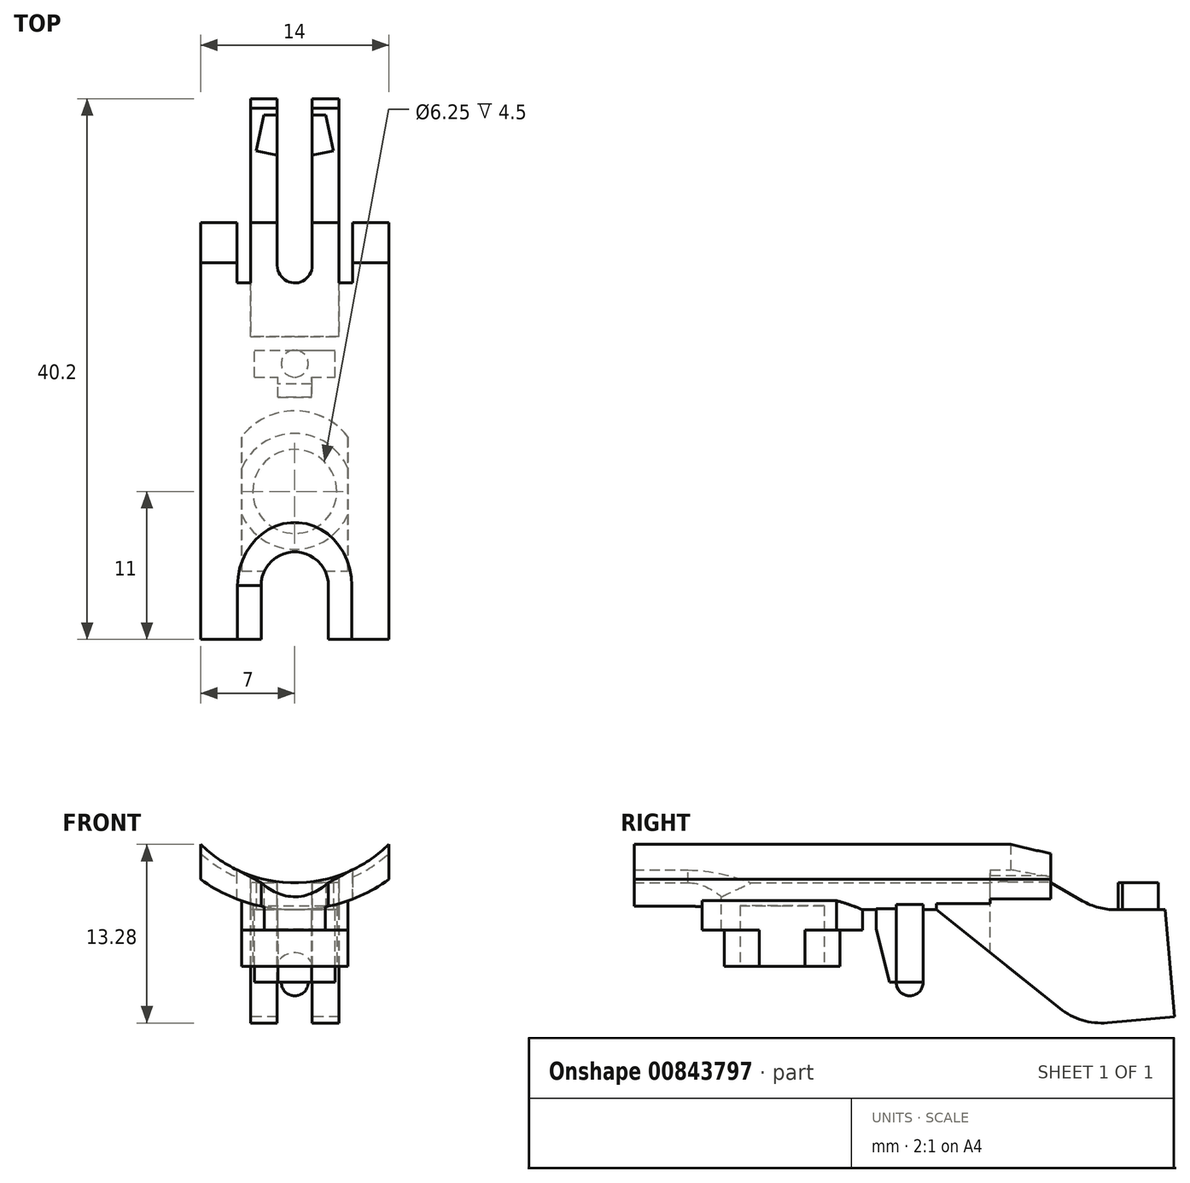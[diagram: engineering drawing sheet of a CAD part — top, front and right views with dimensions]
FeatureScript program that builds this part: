
annotation { "Feature Type Name" : "Feature", "Feature Type Description" : "" }
export const myFeature = defineFeature(function(context is Context, id is Id, definition is map)
    precondition{}
    {
        {
            var Q0;
            Q0=qCreatedBy(makeId("Front.planeOp"),FACE);
            var sketch = newSketch(context, id + "F0", { "sketchPlane" : qUnion([Q0])});
            skArc(sketch, "E0", {"start": v(-7, -7.14) * mm, "mid": v(0, -10) * mm, "end": v(7, -7.14) * mm});
            skLineSegment(sketch, "E1", {"start": v(-7, -11.98) * mm, "end": v(-7, 0) * mm, "construction": true});
            skLineSegment(sketch, "E2", {"start": v(-7, 0) * mm, "end": v(7, 0) * mm, "construction": true});
            skLineSegment(sketch, "E3", {"start": v(7, 0) * mm, "end": v(7, -11.98) * mm, "construction": true});
            skArc(sketch, "E4.0", {"start": v(-7, -9.75) * mm, "mid": v(0, -12) * mm, "end": v(7, -9.75) * mm});
            skLineSegment(sketch, "E5", {"start": v(-7, -9.75) * mm, "end": v(-7, -7.14) * mm});
            skLineSegment(sketch, "E6", {"start": v(7, -7.14) * mm, "end": v(7, -9.75) * mm});
            skSolve(sketch);
        }
        {
            var Q0;
            Q0=makeQuery(id+"F0.imprint","IMPRINT",FACE,{"disambiguationData":[TD([[makeQuery(id+"F0.imprint","IMPRINT",EDGE,{"derivedFrom":sQuery(id+"F0.wireOp",EDGE,"E0")}),-1.0]])]});
            extrude(context, id + "F1", {"entities" : qUnion([Q0]), "endBound" : BoundingType.SYMMETRIC, "depth" : 31 * mm, "offsetDistance" : 25 * mm});
        }
        {
            var Q0;
            Q0=qCreatedBy(makeId("Top.planeOp"),FACE);
            var sketch = newSketch(context, id + "F2", { "sketchPlane" : qUnion([Q0])});
            skArc(sketch, "E7", {"start": v(2.5, -11.5) * mm, "mid": v(0, -9) * mm, "end": v(-2.5, -11.5) * mm});
            skLineSegment(sketch, "E8", {"start": v(-2.5, -11.5) * mm, "end": v(-2.5, -15.5) * mm});
            skLineSegment(sketch, "E9", {"start": v(-2.5, -15.5) * mm, "end": v(2.5, -15.5) * mm});
            skLineSegment(sketch, "E10", {"start": v(2.5, -15.5) * mm, "end": v(2.5, -11.5) * mm});
            skSolve(sketch);
        }
        {
            var Q0;
            Q0=qCreatedBy(makeId("Top.planeOp"),FACE);
            cPlane(context, id + "F3", {"entities" : qUnion([Q0]), "cplaneType" : CPlaneType.OFFSET, "offset" : 10 * mm, "oppositeDirection" : true, "width" : 150 * mm, "height" : 150 * mm});
        }
        {
            var Q0;
            Q0=qCreatedBy(id+"F3.planeOp",FACE);
            var sketch = newSketch(context, id + "F4", { "sketchPlane" : qUnion([Q0])});
            skLineSegment(sketch, "E11", {"start": v(-3.95, -0.43) * mm, "end": v(-3.95, -10.43) * mm});
            skLineSegment(sketch, "E12", {"start": v(-3.95, -10.43) * mm, "end": v(3.95, -10.43) * mm});
            skArc(sketch, "E13", {"start": v(3.95, -0.43) * mm, "mid": v(0, 1.5) * mm, "end": v(-3.95, -0.43) * mm});
            skLineSegment(sketch, "E14", {"start": v(3.95, -0.43) * mm, "end": v(3.95, -10.43) * mm});
            skSolve(sketch);
        }
        {
            var Q0;
            Q0=makeQuery(id+"F4.imprint","IMPRINT",FACE,{"disambiguationData":[TD([[makeQuery(id+"F4.imprint","IMPRINT",EDGE,{"derivedFrom":sQuery(id+"F4.wireOp",EDGE,"E11")}),1.0]])]});
            extrude(context, id + "F5", {"entities" : qUnion([Q0]), "operationType" : NewBodyOperationType.ADD, "oppositeDirection" : true, "depth" : 3.5 * mm, "offsetDistance" : 25 * mm});
        }
        {
            var Q0;
            Q0=makeQuery(id+"F2.imprint","IMPRINT",FACE,{"disambiguationData":[TD([[makeQuery(id+"F2.imprint","IMPRINT",EDGE,{"derivedFrom":sQuery(id+"F2.wireOp",EDGE,"E7")}),1.0]])]});
            extrude(context, id + "F6", {"entities" : qUnion([Q0]), "operationType" : NewBodyOperationType.REMOVE, "endBound" : BoundingType.THROUGH_ALL, "oppositeDirection" : true, "depth" : 25 * mm, "offsetDistance" : 25 * mm});
        }
        {
            var Q0;
            Q0=makeQuery(id+"F6.boolean.opBoolean","INTERSECT",EDGE,{"derivedFrom":[makeQuery(id+"F1.opExtrude","SWEPT_FACE",FACE,{"disambiguationData":[OSD([sQuery(id+"F0.wireOp",EDGE,"E0")])]}),makeQuery(id+"F6.opExtrude","SWEPT_FACE",FACE,{"disambiguationData":[OSD([sQuery(id+"F2.wireOp",EDGE,"E8")])]})]});
            var Q1;
            Q1=makeQuery(id+"F6.boolean.opBoolean","INTERSECT",EDGE,{"derivedFrom":[makeQuery(id+"F1.opExtrude","SWEPT_FACE",FACE,{"disambiguationData":[OSD([sQuery(id+"F0.wireOp",EDGE,"E0")])]}),makeQuery(id+"F6.opExtrude","SWEPT_FACE",FACE,{"disambiguationData":[OSD([sQuery(id+"F2.wireOp",EDGE,"E7")])]})]});
            var Q2;
            Q2=makeQuery(id+"F6.boolean.opBoolean","INTERSECT",EDGE,{"derivedFrom":[makeQuery(id+"F1.opExtrude","SWEPT_FACE",FACE,{"disambiguationData":[OSD([sQuery(id+"F0.wireOp",EDGE,"E0")])]}),makeQuery(id+"F6.opExtrude","SWEPT_FACE",FACE,{"disambiguationData":[OSD([sQuery(id+"F2.wireOp",EDGE,"E10")])]})]});
            chamfer(context, id + "F7", {"entities" : qUnion([Q0, Q1, Q2]), "chamferType" : ChamferType.TWO_OFFSETS, "width1" : .5 * mm, "oppositeDirection" : false, "width2" : 2 * mm, "tangentPropagation" : true});
        }
        {
            var Q0;
            Q0=qCreatedBy(id+"F3.planeOp",FACE);
            var sketch = newSketch(context, id + "F8", { "sketchPlane" : qUnion([Q0])});
            skLineSegment(sketch, "E15.bottom", {"start": v(-3, 6) * mm, "end": v(3, 6) * mm});
            skLineSegment(sketch, "E15.top", {"start": v(-3, 4) * mm, "end": v(-1.25, 4) * mm});
            skLineSegment(sketch, "E15.left", {"start": v(-3, 6) * mm, "end": v(-3, 4) * mm});
            skLineSegment(sketch, "E15.right", {"start": v(3, 6) * mm, "end": v(3, 4) * mm});
            skLineSegment(sketch, "E16", {"start": v(1.25, 4) * mm, "end": v(1.25, 2.5) * mm});
            skLineSegment(sketch, "E17", {"start": v(1.25, 2.5) * mm, "end": v(-1.25, 2.5) * mm});
            skLineSegment(sketch, "E18", {"start": v(-1.25, 2.5) * mm, "end": v(-1.25, 4) * mm});
            skLineSegment(sketch, "E19.trimOffspring", {"start": v(1.25, 4) * mm, "end": v(3, 4) * mm});
            skSolve(sketch);
        }
        {
            var Q0;
            Q0 = qSketchRegion(id + "F8", true);
            extrude(context, id + "F9", {"entities" : qUnion([Q0]), "operationType" : NewBodyOperationType.ADD, "oppositeDirection" : true, "depth" : 7.4 * mm, "offsetDistance" : 25 * mm});
        }
        {
            var Q0;
            Q0=qCreatedBy(makeId("Right.planeOp"),FACE);
            var sketch = newSketch(context, id + "F10", { "sketchPlane" : qUnion([Q0])});
            skLineSegment(sketch, "E20", {"start": v(15.5, -10) * mm, "end": v(19, -12) * mm});
            skLineSegment(sketch, "E21", {"start": v(19, -12) * mm, "end": v(24, -12) * mm});
            skLineSegment(sketch, "E22", {"start": v(24, -12) * mm, "end": v(24.7, -19.97) * mm});
            skLineSegment(sketch, "E23", {"start": v(24.7, -19.97) * mm, "end": v(17.72, -20.58) * mm});
            skLineSegment(sketch, "E24", {"start": v(17.72, -20.58) * mm, "end": v(7, -12) * mm});
            skLineSegment(sketch, "E25", {"start": v(7, -12) * mm, "end": v(7, -10) * mm});
            skLineSegment(sketch, "E26", {"start": v(7, -10) * mm, "end": v(15.5, -10) * mm});
            skSolve(sketch);
        }
        {
            var Q0;
            Q0=makeQuery(id+"F10.imprint","IMPRINT",FACE,{"disambiguationData":[TD([[makeQuery(id+"F10.imprint","IMPRINT",EDGE,{"derivedFrom":sQuery(id+"F10.wireOp",EDGE,"E20")}),-1.0]])]});
            extrude(context, id + "F11", {"entities" : qUnion([Q0]), "operationType" : NewBodyOperationType.ADD, "endBound" : BoundingType.SYMMETRIC, "depth" : 6.6 * mm, "offsetDistance" : 25 * mm});
        }
        {
            var Q0;
            Q0=qCreatedBy(makeId("Top.planeOp"),FACE);
            var sketch = newSketch(context, id + "F12", { "sketchPlane" : qUnion([Q0])});
            skLineSegment(sketch, "E27.bottom", {"start": v(-4.3, 11) * mm, "end": v(-3.3, 11) * mm});
            skLineSegment(sketch, "E27.top", {"start": v(-4.3, 20.5) * mm, "end": v(-3.3, 20.5) * mm});
            skLineSegment(sketch, "E27.left", {"start": v(-4.3, 11) * mm, "end": v(-4.3, 20.5) * mm});
            skLineSegment(sketch, "E27.right", {"start": v(-3.3, 11) * mm, "end": v(-3.3, 20.5) * mm});
            skLineSegment(sketch, "E28.bottom", {"start": v(4.3, 20.5) * mm, "end": v(3.3, 20.5) * mm});
            skLineSegment(sketch, "E28.top", {"start": v(4.3, 11) * mm, "end": v(3.3, 11) * mm});
            skLineSegment(sketch, "E28.left", {"start": v(4.3, 20.5) * mm, "end": v(4.3, 11) * mm});
            skLineSegment(sketch, "E28.right", {"start": v(3.3, 20.5) * mm, "end": v(3.3, 11) * mm});
            skLineSegment(sketch, "E29", {"start": v(3.3, 11) * mm, "end": v(0, 11) * mm, "construction": true});
            skLineSegment(sketch, "E30", {"start": v(0, 11) * mm, "end": v(-3.3, 11) * mm, "construction": true});
            skArc(sketch, "E31", {"start": v(-1.3, 12.3) * mm, "mid": v(0, 11) * mm, "end": v(1.3, 12.3) * mm});
            skLineSegment(sketch, "E32", {"start": v(-1.3, 12.3) * mm, "end": v(-1.3, 29.7) * mm});
            skLineSegment(sketch, "E33", {"start": v(1.3, 12.3) * mm, "end": v(1.3, 29.7) * mm});
            skLineSegment(sketch, "E34", {"start": v(1.3, 29.7) * mm, "end": v(-1.3, 29.7) * mm});
            skSolve(sketch);
        }
        {
            var Q0;
            Q0=makeQuery(id+"F12.imprint","IMPRINT",FACE,{"disambiguationData":[TD([[makeQuery(id+"F12.imprint","IMPRINT",EDGE,{"derivedFrom":sQuery(id+"F12.wireOp",EDGE,"E28.bottom")}),1.0]])]});
            var Q1;
            Q1=makeQuery(id+"F12.imprint","IMPRINT",FACE,{"disambiguationData":[TD([[makeQuery(id+"F12.imprint","IMPRINT",EDGE,{"derivedFrom":sQuery(id+"F12.wireOp",EDGE,"E31")}),1.0]])]});
            var Q2;
            Q2=makeQuery(id+"F12.imprint","IMPRINT",FACE,{"disambiguationData":[TD([[makeQuery(id+"F12.imprint","IMPRINT",EDGE,{"derivedFrom":sQuery(id+"F12.wireOp",EDGE,"E27.bottom")}),1.0]])]});
            extrude(context, id + "F13", {"entities" : qUnion([Q0, Q1, Q2]), "operationType" : NewBodyOperationType.REMOVE, "endBound" : BoundingType.THROUGH_ALL, "oppositeDirection" : true, "depth" : 25 * mm, "offsetDistance" : 25 * mm});
        }
        {
            var Q0;
            {var subQ1=sQuery(id+"F10.wireOp",EDGE,"E21");Q0=makeQuery(id+"F13.boolean.opBoolean","SPLIT",FACE,{"disambiguationData":[TD([makeQuery(id+"F13.opExtrude","SWEPT_FACE",FACE,{"disambiguationData":[OSD([sQuery(id+"F12.wireOp",EDGE,"E28.right")])]})])],"derivedFrom":makeQuery(id+"F11.opExtrude","SWEPT_FACE",FACE,{"disambiguationData":[OSD([subQ1])]})});}
            var sketch = newSketch(context, id + "F14", { "sketchPlane" : qUnion([Q0])});
            skLineSegment(sketch, "E35", {"start": v(1.3, 20.5) * mm, "end": v(2.87, 20.83) * mm});
            skLineSegment(sketch, "E36", {"start": v(2.87, 20.83) * mm, "end": v(2.3, 23.5) * mm});
            skLineSegment(sketch, "E37", {"start": v(2.3, 23.5) * mm, "end": v(1.3, 23.5) * mm});
            skLineSegment(sketch, "E38", {"start": v(1.3, 23.5) * mm, "end": v(1.3, 20.5) * mm});
            skLineSegment(sketch, "E39.MirrorCS", {"start": v(-1.3, 20.5) * mm, "end": v(-2.87, 20.83) * mm});
            skLineSegment(sketch, "E40.MirrorCS", {"start": v(-1.3, 23.5) * mm, "end": v(-1.3, 20.5) * mm});
            skLineSegment(sketch, "E41.MirrorCS", {"start": v(-2.87, 20.83) * mm, "end": v(-2.3, 23.5) * mm});
            skLineSegment(sketch, "E42.MirrorCS", {"start": v(-2.3, 23.5) * mm, "end": v(-1.3, 23.5) * mm});
            skSolve(sketch);
        }
        {
            var Q0;
            Q0=makeQuery(id+"F14.imprint","IMPRINT",FACE,{"disambiguationData":[TD([[makeQuery(id+"F14.imprint","IMPRINT",EDGE,{"derivedFrom":sQuery(id+"F14.wireOp",EDGE,"E35")}),1.0]])]});
            var Q1;
            Q1=makeQuery(id+"F14.imprint","IMPRINT",FACE,{"disambiguationData":[TD([[makeQuery(id+"F14.imprint","IMPRINT",EDGE,{"derivedFrom":sQuery(id+"F14.wireOp",EDGE,"E39.MirrorCS")}),-1.0]])]});
            extrude(context, id + "F15", {"entities" : qUnion([Q0, Q1]), "operationType" : NewBodyOperationType.ADD, "depth" : 2 * mm, "offsetDistance" : 25 * mm});
        }
        {
            var Q0;
            Q0=qCreatedBy(makeId("Right.planeOp"),FACE);
            var sketch = newSketch(context, id + "F16", { "sketchPlane" : qUnion([Q0])});
            skArc(sketch, "E43", {"start": v(5, -18.4) * mm, "mid": v(6, -17.4) * mm, "end": v(5, -16.4) * mm});
            skLineSegment(sketch, "E44", {"start": v(5, -18.4) * mm, "end": v(5, -16.4) * mm});
            skSolve(sketch);
        }
        {
            var Q0;
            Q0=makeQuery(id+"F16.imprint","IMPRINT",FACE,{"disambiguationData":[TD([[makeQuery(id+"F16.imprint","IMPRINT",EDGE,{"derivedFrom":sQuery(id+"F16.wireOp",EDGE,"E43")}),1.0]])]});
            var Q1;
            Q1=sQuery(id+"F16.wireOp",EDGE,"E44");
            revolve(context, id + "F17", {"operationType" : NewBodyOperationType.ADD, "surfaceOperationType" : NewSurfaceOperationType.NEW, "entities" : qUnion([Q0]), "axis" : qUnion([Q1]), "revolveType" : RevolveType.FULL});
        }
        {
            var Q0;
            Q0=makeQuery(id+"F5.opExtrude","CAP_FACE",FACE,{"disambiguationData":[OSD([sQuery(id+"F4.wireOp",EDGE,"E11"),sQuery(id+"F4.wireOp",EDGE,"E12"),sQuery(id+"F4.wireOp",EDGE,"E13"),sQuery(id+"F4.wireOp",EDGE,"E14")])],"isStart":false});
            var sketch = newSketch(context, id + "F18", { "sketchPlane" : qUnion([Q0])});
            skArc(sketch, "E45", {"start": v(3.95, 6.2) * mm, "mid": v(0, 8.8) * mm, "end": v(-3.95, 6.2) * mm});
            skLineSegment(sketch, "E46", {"start": v(3.95, 6.2) * mm, "end": v(3.95, 2.8) * mm});
            skLineSegment(sketch, "E47", {"start": v(-3.95, 2.8) * mm, "end": v(-3.95, 6.2) * mm});
            skArc(sketch, "E48.trimOffspring", {"start": v(-3.95, 2.8) * mm, "mid": v(0, 0.2) * mm, "end": v(3.95, 2.8) * mm});
            skSolve(sketch);
        }
        {
            var Q0;
            Q0=makeQuery(id+"F18.imprint","IMPRINT",FACE,{"disambiguationData":[TD([[makeQuery(id+"F18.imprint","IMPRINT",EDGE,{"derivedFrom":sQuery(id+"F18.wireOp",EDGE,"E45")}),1.0]])]});
            extrude(context, id + "F19", {"entities" : qUnion([Q0]), "operationType" : NewBodyOperationType.ADD, "depth" : 2.7 * mm, "offsetDistance" : 25 * mm});
        }
        {
            var Q0;
            Q0=makeQuery(id+"F9.opExtrude","CAP_EDGE",EDGE,{"disambiguationData":[OSD([sQuery(id+"F8.wireOp",EDGE,"E17")])],"isStart":false});
            chamfer(context, id + "F20", {"entities" : qUnion([Q0]), "chamferType" : ChamferType.TWO_OFFSETS, "width1" : 1 * mm, "oppositeDirection" : false, "width2" : 4 * mm, "tangentPropagation" : true});
        }
        {
            var Q0;
            Q0=makeQuery(id+"F19.opExtrude","CAP_FACE",FACE,{"disambiguationData":[OSD([sQuery(id+"F18.wireOp",EDGE,"E45"),sQuery(id+"F18.wireOp",EDGE,"E46"),sQuery(id+"F18.wireOp",EDGE,"E47"),sQuery(id+"F18.wireOp",EDGE,"E48.trimOffspring")])],"isStart":false});
            var sketch = newSketch(context, id + "F21", { "sketchPlane" : qUnion([Q0])});
            skCircle(sketch, "E49", {"center": v(0, 4.5) * mm, "radius": 3.12 * mm});
            skSolve(sketch);
        }
        {
            var Q0;
            Q0=makeQuery(id+"F21.imprint","IMPRINT",FACE,{"disambiguationData":[TD([[makeQuery(id+"F21.imprint","IMPRINT",EDGE,{"derivedFrom":sQuery(id+"F21.wireOp",EDGE,"E49")}),1.0]])]});
            extrude(context, id + "F22", {"entities" : qUnion([Q0]), "operationType" : NewBodyOperationType.REMOVE, "oppositeDirection" : true, "depth" : 4.5 * mm, "offsetDistance" : 25 * mm});
        }
        {
            var Q0;
            {var subQ0=sQuery(id+"F0.wireOp",EDGE,"E0");var subQ2=sQuery(id+"F0.wireOp",EDGE,"E5");var subQ4=makeQuery(id+"F1.opExtrude","SWEPT_FACE",FACE,{"disambiguationData":[OSD([subQ2])]});Q0=makeQuery(id+"F13.boolean.opBoolean","SPLIT",EDGE,{"disambiguationData":[TD([subQ4])],"derivedFrom":makeQuery(id+"F11.boolean.opBoolean","SPLIT",EDGE,{"disambiguationData":[TD([subQ4])],"derivedFrom":makeQuery(id+"F1.opExtrude","CAP_EDGE",EDGE,{"disambiguationData":[OSD([subQ0])],"isStart":true})})});}
            var Q1;
            {var subQ0=sQuery(id+"F0.wireOp",EDGE,"E0");var subQ2=sQuery(id+"F0.wireOp",EDGE,"E6");var subQ3=makeQuery(id+"F1.opExtrude","SWEPT_FACE",FACE,{"disambiguationData":[OSD([subQ2])]});Q1=makeQuery(id+"F13.boolean.opBoolean","SPLIT",EDGE,{"disambiguationData":[TD([subQ3])],"derivedFrom":makeQuery(id+"F11.boolean.opBoolean","SPLIT",EDGE,{"disambiguationData":[TD([subQ3])],"derivedFrom":makeQuery(id+"F1.opExtrude","CAP_EDGE",EDGE,{"disambiguationData":[OSD([subQ0])],"isStart":true})})});}
            chamfer(context, id + "F23", {"entities" : qUnion([Q0, Q1]), "chamferType" : ChamferType.TWO_OFFSETS, "width1" : .5 * mm, "oppositeDirection" : false, "width2" : 3 * mm, "tangentPropagation" : true});
        }
        {
            var Q0;
            {var subQ0=sQuery(id+"F10.wireOp",EDGE,"E23");var subQ1=sQuery(id+"F10.wireOp",EDGE,"E24");Q0=makeQuery(id+"F13.boolean.opBoolean","SPLIT",EDGE,{"disambiguationData":[TD([makeQuery(id+"F13.opExtrude","SWEPT_FACE",FACE,{"disambiguationData":[OSD([sQuery(id+"F12.wireOp",EDGE,"E27.right")])]})])],"derivedFrom":makeQuery(id+"F11.opExtrude","SWEPT_EDGE",EDGE,{"disambiguationData":[OSD([subQ0,subQ1])]})});}
            var Q1;
            {var subQ0=sQuery(id+"F10.wireOp",EDGE,"E24");var subQ1=sQuery(id+"F10.wireOp",EDGE,"E23");Q1=makeQuery(id+"F13.boolean.opBoolean","SPLIT",EDGE,{"disambiguationData":[TD([makeQuery(id+"F13.opExtrude","SWEPT_FACE",FACE,{"disambiguationData":[OSD([sQuery(id+"F12.wireOp",EDGE,"E28.right")])]})])],"derivedFrom":makeQuery(id+"F11.opExtrude","SWEPT_EDGE",EDGE,{"disambiguationData":[OSD([subQ1,subQ0])]})});}
            fillet(context, id + "F24", {"entities" : qUnion([Q0, Q1]), "radius" : 5 * mm, "tangentPropagation" : true, "allowEdgeOverflow" : false});
        }
        {
            var Q0;
            {var subQ0=sQuery(id+"F10.wireOp",EDGE,"E21");var subQ1=sQuery(id+"F10.wireOp",EDGE,"E20");Q0=makeQuery(id+"F13.boolean.opBoolean","SPLIT",EDGE,{"disambiguationData":[TD([makeQuery(id+"F13.opExtrude","SWEPT_FACE",FACE,{"disambiguationData":[OSD([sQuery(id+"F12.wireOp",EDGE,"E28.right")])]})])],"derivedFrom":makeQuery(id+"F11.opExtrude","SWEPT_EDGE",EDGE,{"disambiguationData":[OSD([subQ1,subQ0])]})});}
            var Q1;
            {var subQ0=sQuery(id+"F10.wireOp",EDGE,"E21");var subQ1=sQuery(id+"F10.wireOp",EDGE,"E20");Q1=makeQuery(id+"F13.boolean.opBoolean","SPLIT",EDGE,{"disambiguationData":[TD([makeQuery(id+"F13.opExtrude","SWEPT_FACE",FACE,{"disambiguationData":[OSD([sQuery(id+"F12.wireOp",EDGE,"E27.right")])]})])],"derivedFrom":makeQuery(id+"F11.opExtrude","SWEPT_EDGE",EDGE,{"disambiguationData":[OSD([subQ1,subQ0])]})});}
            fillet(context, id + "F25", {"entities" : qUnion([Q0, Q1]), "radius" : 5 * mm, "tangentPropagation" : true, "allowEdgeOverflow" : false});
        }
    });
